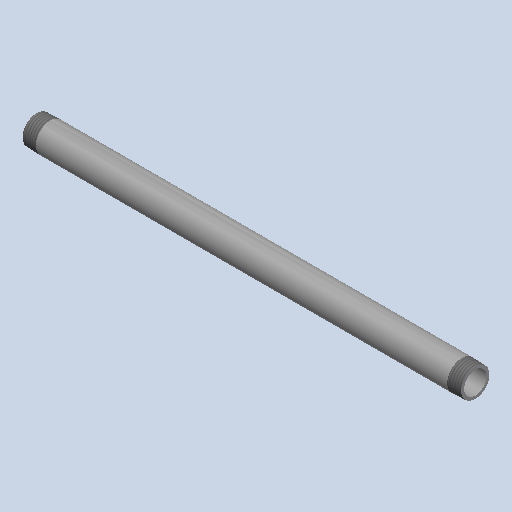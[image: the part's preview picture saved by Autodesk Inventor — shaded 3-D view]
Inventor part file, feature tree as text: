
AUTODESK INVENTOR PART (.ipt)
format: ipt  version: 2025 (Build 290162000, 162)  size: 168,960 bytes
history: native  units: mm (DEFAULTED — no unit token found)
features: other x8, revolve x1
ambient origin geometry x8: Origin, YZ Plane, XZ Plane, XY Plane, X Axis, Y Axis, Z Axis, Center Point
bodies: Solid1 (feature_tree)
feature tree (9):
  revolve  "Revolution1"  [1 undecoded]
  other  "Work Axis1"
  other  "Work Point5"
  other  "Work Axis2"
  other  "Work Point6"
  other  "Work Axis3"
  other  "Work Axis4"
  other  "Work Point7"
  other  "Work Point8"
note: 1 required parameter value undecoded (feature->parameter linkage not recoverable at this tier; creation-order binding heuristic only, values carry confidence <= 0.55)
